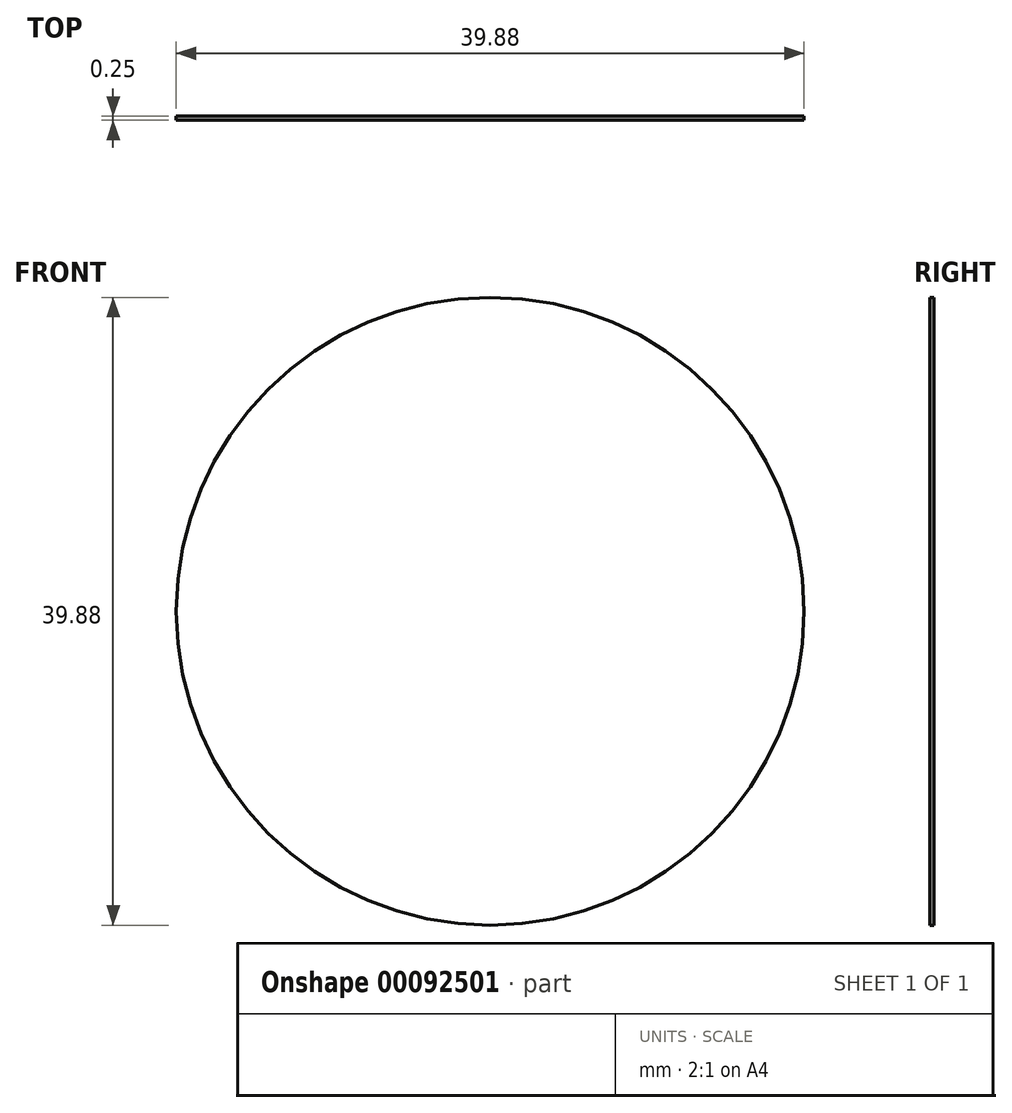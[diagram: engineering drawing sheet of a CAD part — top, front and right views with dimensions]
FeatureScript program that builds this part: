
annotation { "Feature Type Name" : "Feature", "Feature Type Description" : "" }
export const myFeature = defineFeature(function(context is Context, id is Id, definition is map)
    precondition{}
    {
        {
            var Q0;
            Q0=qCreatedBy(makeId("Front.planeOp"),FACE);
            var sketch = newSketch(context, id + "F0", { "sketchPlane" : qUnion([Q0])});
            skCircle(sketch, "E0", {"center": v(0, 0) * mm, "radius": 19.94 * mm});
            skSolve(sketch);
        }
        {
            var Q0;
            Q0 = qSketchRegion(id + "F0", true);
            extrude(context, id + "F1", {"entities" : qUnion([Q0]), "depth" : 0.25 * mm});
        }
    });
